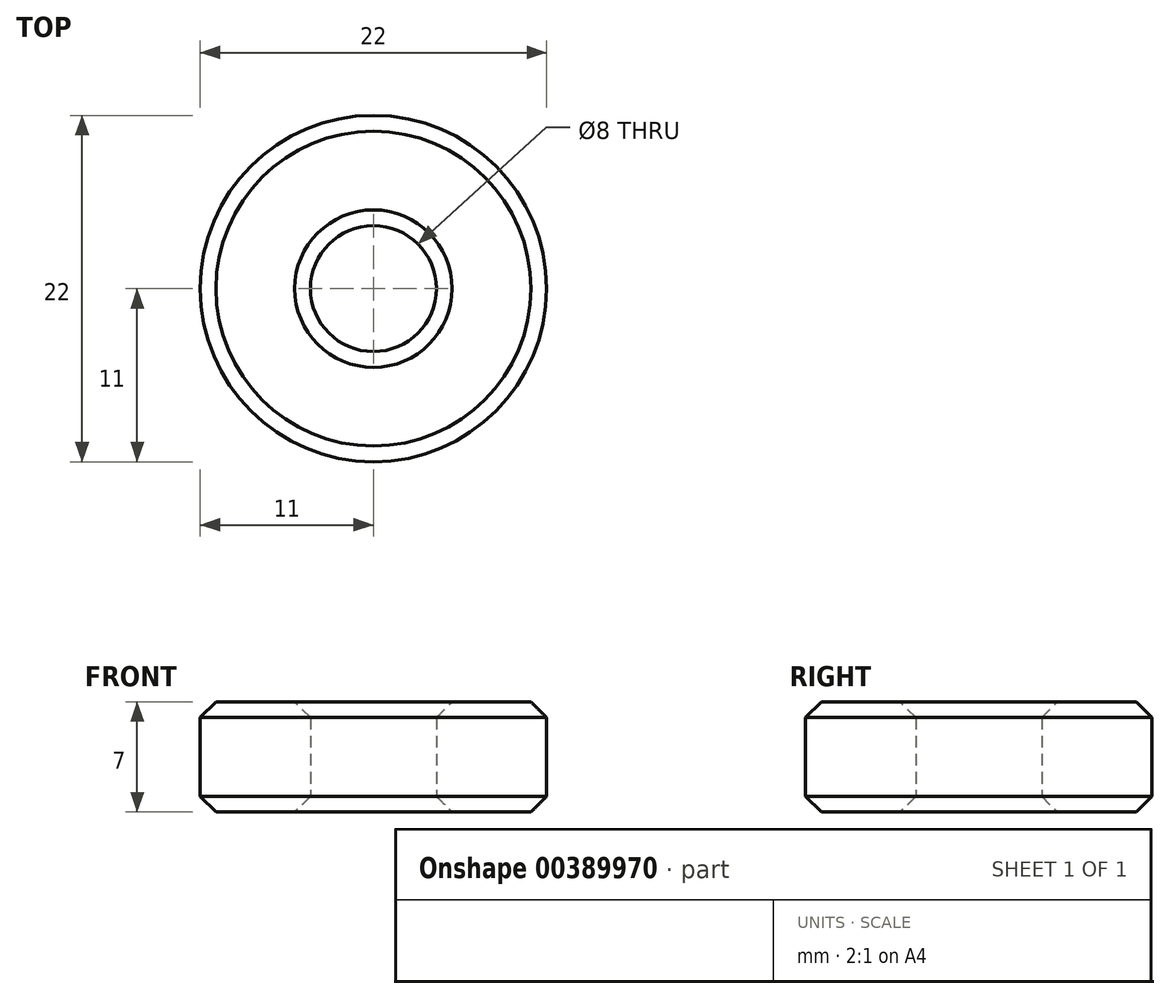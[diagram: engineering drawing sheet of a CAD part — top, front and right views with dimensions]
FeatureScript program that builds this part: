
annotation { "Feature Type Name" : "Feature", "Feature Type Description" : "" }
export const myFeature = defineFeature(function(context is Context, id is Id, definition is map)
    precondition{}
    {
        {
            var Q0;
            Q0=qCreatedBy(makeId("Top.planeOp"),FACE);
            var sketch = newSketch(context, id + "F0", { "sketchPlane" : qUnion([Q0])});
            skCircle(sketch, "E0", {"center": v(0, 0) * mm, "radius": 11 * mm});
            skCircle(sketch, "E1", {"center": v(0, 0) * mm, "radius": 4 * mm});
            skSolve(sketch);
        }
        {
            var Q0;
            Q0=makeQuery(id+"F0.imprint","IMPRINT",FACE,{"disambiguationData":[TD([[makeQuery(id+"F0.imprint","IMPRINT",EDGE,{"derivedFrom":sQuery(id+"F0.wireOp",EDGE,"E0")}),1.0]])]});
            extrude(context, id + "F1", {"entities" : qUnion([Q0]), "depth" : 7 * mm});
        }
        {
            var Q0;
            Q0=makeQuery(id+"F1.opExtrude","CAP_EDGE",EDGE,{"disambiguationData":[OSD([sQuery(id+"F0.wireOp",EDGE,"E0")])],"isStart":false});
            var Q1;
            Q1=makeQuery(id+"F1.opExtrude","CAP_EDGE",EDGE,{"disambiguationData":[OSD([sQuery(id+"F0.wireOp",EDGE,"E0")])],"isStart":true});
            var Q2;
            Q2=makeQuery(id+"F1.opExtrude","SWEPT_FACE",FACE,{"disambiguationData":[OSD([sQuery(id+"F0.wireOp",EDGE,"E1")])]});
            chamfer(context, id + "F2", {"entities" : qUnion([Q0, Q1, Q2]), "width" : 1 * mm, "tangentPropagation" : true});
        }
    });
